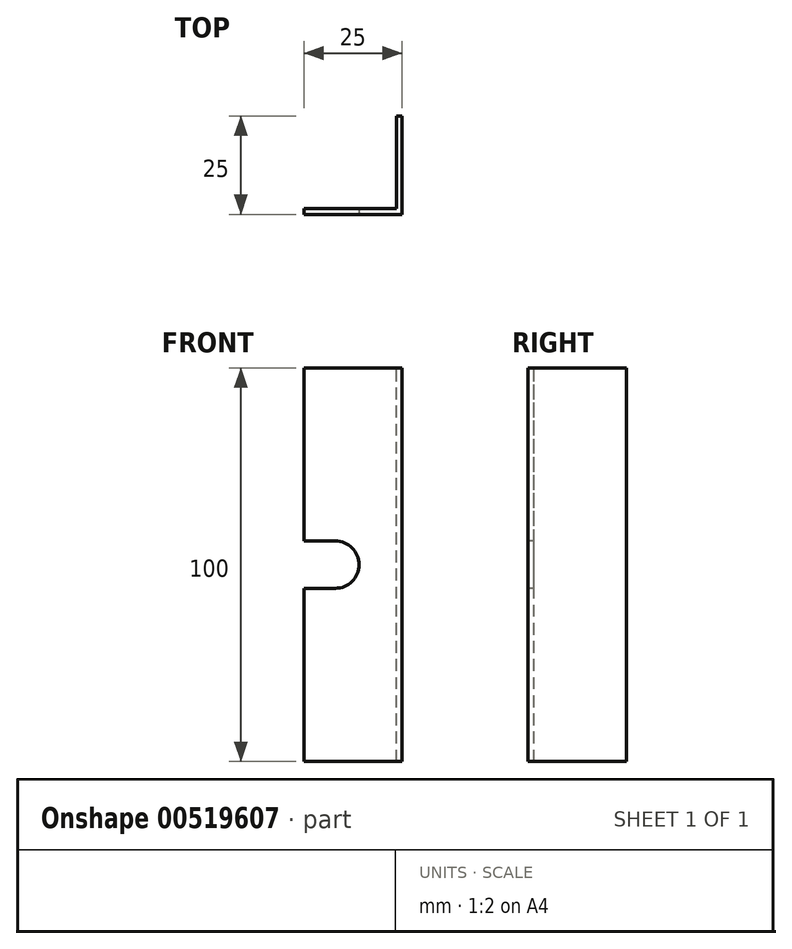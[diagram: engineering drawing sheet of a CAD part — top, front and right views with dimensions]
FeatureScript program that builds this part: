
annotation { "Feature Type Name" : "Feature", "Feature Type Description" : "" }
export const myFeature = defineFeature(function(context is Context, id is Id, definition is map)
    precondition{}
    {
        {
            var Q0;
            Q0=qCreatedBy(makeId("Top.planeOp"),FACE);
            var sketch = newSketch(context, id + "F0", { "sketchPlane" : qUnion([Q0])});
            skLineSegment(sketch, "E0.bottom", {"start": v(12.5, 0.75) * mm, "end": v(-12.5, 0.75) * mm});
            skLineSegment(sketch, "E0.top", {"start": v(12.5, -0.75) * mm, "end": v(-12.5, -0.75) * mm});
            skLineSegment(sketch, "E0.left", {"start": v(12.5, 0.75) * mm, "end": v(12.5, -0.75) * mm});
            skLineSegment(sketch, "E0.right", {"start": v(-12.5, 0.75) * mm, "end": v(-12.5, -0.75) * mm});
            skPoint(sketch, "E0.middle", {"position": v(0, 0) * mm});
            skLineSegment(sketch, "E1.bottom", {"start": v(12.5, -0.75) * mm, "end": v(11, -0.75) * mm});
            skLineSegment(sketch, "E1.top", {"start": v(12.5, 24.25) * mm, "end": v(11, 24.25) * mm});
            skLineSegment(sketch, "E1.left", {"start": v(12.5, -0.75) * mm, "end": v(12.5, 24.25) * mm});
            skLineSegment(sketch, "E1.right", {"start": v(11, -0.75) * mm, "end": v(11, 24.25) * mm});
            skSolve(sketch);
        }
        {
            var Q0;
            Q0=qSketchRegion(id+"F0",true);
            extrude(context, id + "F1", {"entities" : qUnion([Q0]), "oppositeDirection" : true, "depth" : 100 * mm, "offsetDistance" : 25 * mm});
        }
        {
            var Q0;
            Q0=makeQuery(id+"F1.opExtrude","SWEPT_FACE",FACE,{"disambiguationData":[OSD([sQuery(id+"F0.wireOp",EDGE,"E0.top"),sQuery(id+"F0.wireOp",EDGE,"E1.bottom")])]});
            var sketch = newSketch(context, id + "F2", { "sketchPlane" : qUnion([Q0])});
            skArc(sketch, "E2", {"start": v(-4.5, -56) * mm, "mid": v(1.5, -50) * mm, "end": v(-4.5, -44) * mm});
            skLineSegment(sketch, "E3", {"start": v(-4.5, -44) * mm, "end": v(-12.5, -44) * mm});
            skLineSegment(sketch, "E4", {"start": v(-4.5, -56) * mm, "end": v(-12.5, -56) * mm});
            skSolve(sketch);
        }
        {
            var Q0;
            Q0 = qSketchRegion(id + "F2", true);
            var Q1;
            Q1=makeQuery(id+"F2.imprint","IMPRINT",FACE,{"disambiguationData":[TD([[makeQuery(id+"F2.imprint","IMPRINT",EDGE,{"derivedFrom":sQuery(id+"F2.wireOp",EDGE,"E2")}),1.0]])]});
            extrude(context, id + "F3", {"entities" : qUnion([Q0, Q1]), "operationType" : NewBodyOperationType.REMOVE, "oppositeDirection" : true, "depth" : 1.5 * mm, "offsetDistance" : 25 * mm});
        }
    });
